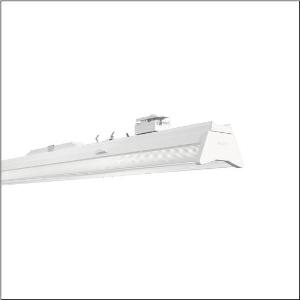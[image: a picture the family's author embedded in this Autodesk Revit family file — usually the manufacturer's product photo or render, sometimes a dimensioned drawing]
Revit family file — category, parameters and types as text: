
# Revit family: licross_r__21_performance_mo_52tm167n46xg_7cd2
name_source: partatom
category: Lighting Fixtures
units: mm (PartAtom-declared; Revit-internal decimal feet)

## family parameters
Cut with Voids When Loaded = No
Host = Face
Light Source = No
Part Type = Normal
Room Calculation Point = No
Round Connector Dimension = Use Diameter
Shared = No

## types (1)
- Licross® 21 Performance MO (1 x LED, 6000 lm, 32.4 W, 4000K)
    Apparent Load = 32 VA
    CIE Flux Codes = 66 88 96 79 100
    Color Rendering = 80
    Color Temperature = 4000K
    Default Elevation = 1800 mm
    Description = Licross® 21 Performance MO, luminaire insert, of sheet steel, galvanised, coil coated, white, length: 1.500mm, width: 120mm, height: 123mm, LED rated luminous flux: 6.000lm, light colour: 840, control gear: ON/OFF, with plug, 3-pole, with phase selection, mains connection: 220..240V, AC, 50/60Hz, rated input power: 32W, halogen-free wiring, primary light control with lens, of plastic, primary optical cover: cover, of PMMA, light emission: direct/indirect distribution, primary light characteristic: symmetric, protection rating (complete): IP40, insulation class (complete): insulation class I (protective earthing), certification: CE, ENEC, UKCA, protection symbol: D if used in an environment without relevant dust loads with corresponding accessories, impact resistance: IK06, permissible ambient temperature for indoor applications: -35..+50°C, corresponds to IFS (International Featured Standards) requirements for safety and quality in the food industry, reducing of maximum allowable ambient temperature of 5°C with ceiling mounting, LABS conformity tested according to VDMA 24364:2018-05, packaging unit: 1 piece
    Height = 114 mm
    Lamp = 1 x LED
    Lamp Light Flux = 6000 lm
    Lamp Power = 32.4 W
    Lamp count = 1
    Length = 1500 mm
    Luminous efficacy = 185 lm/W
    Manufacturer = Siteco
    ModVariant = No
    Model = 52TM167N46XG
    Mounting Place = Ceiling
    Mounting Type = Pendant
    Number of Poles = 1
    OnlyDefault = Yes
    Power Factor = 1
    Product Name = Licross® 21 Performance MO
    Product group = luminaire insert
    ProductGroupID = 901
    Protection Class = Protection class I
    Protection Degree = IP 40
    RLX_Detail_Level = 1
    RLX_Emergency_Light_Flux = 0 lm
    RLX_Emergency_Type = 0
    RLX_Emergency_Type_DB = No
    RlxData = <blob elided: 30385 chars, md5=ade3547d>
    Socket = socket
    Standby Power = 0 W
    System Light Flux = 6000 lm
    System Power = 32 W
    Type Comments = Product without accessories
    Type Image = l_1256138.jpg
    URL = http://relux.com
    VarID = ---
    Voltage = 0 V
    Weight = 0.00 kg
    Width = 120 mm

## geometry (parser evidence)
native form markers: Blend x4, Sweep x12
no freeform markers — native parametric forms only
